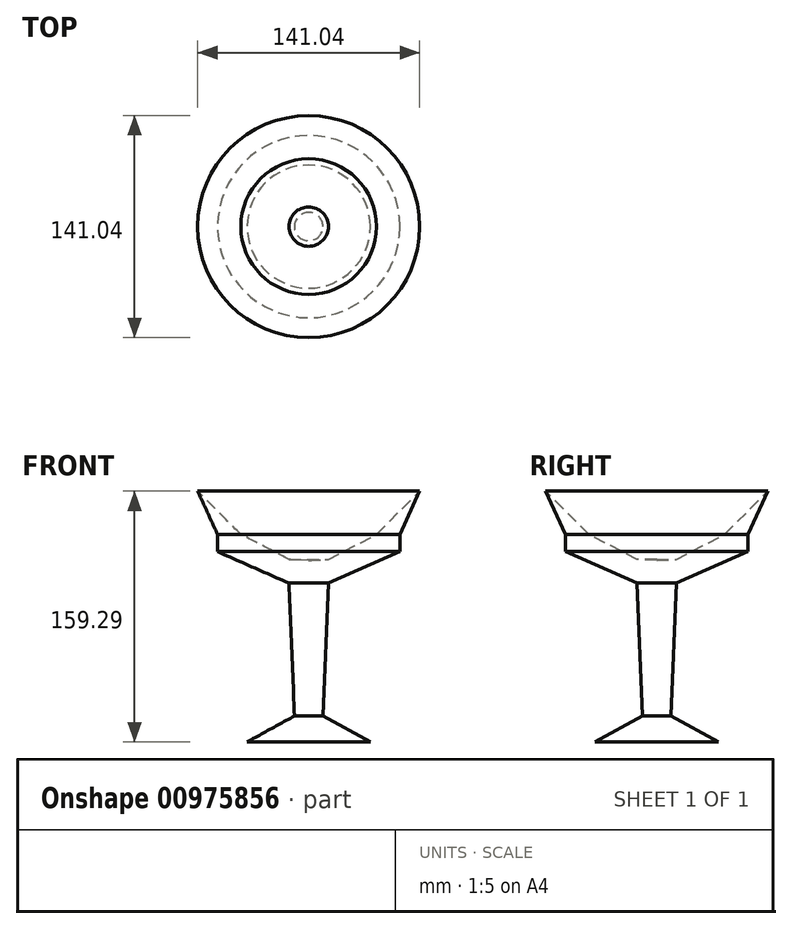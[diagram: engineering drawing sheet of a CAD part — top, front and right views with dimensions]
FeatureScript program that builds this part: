
annotation { "Feature Type Name" : "Feature", "Feature Type Description" : "" }
export const myFeature = defineFeature(function(context is Context, id is Id, definition is map)
    precondition{}
    {
        {
            var Q0;
            Q0=qCreatedBy(makeId("Front.planeOp"),FACE);
            var sketch = newSketch(context, id + "F0", { "sketchPlane" : qUnion([Q0])});
            skLineSegment(sketch, "E0", {"start": v(0, 79.46) * mm, "end": v(0, -77.08) * mm, "construction": true});
            skLineSegment(sketch, "E1", {"start": v(0, -61.15) * mm, "end": v(-39.11, -61.15) * mm});
            skLineSegment(sketch, "E2", {"start": v(-39.11, -61.15) * mm, "end": v(-9.05, -44.68) * mm});
            skLineSegment(sketch, "E3", {"start": v(-9.05, -44.68) * mm, "end": v(-12.5, 39.68) * mm});
            skLineSegment(sketch, "E4", {"start": v(-12.5, 39.68) * mm, "end": v(-57.9, 59.69) * mm});
            skLineSegment(sketch, "E5", {"start": v(-57.9, 59.69) * mm, "end": v(-57.9, 70.67) * mm});
            skLineSegment(sketch, "E6", {"start": v(-57.9, 70.67) * mm, "end": v(-70.52, 98.14) * mm});
            skLineSegment(sketch, "E7", {"start": v(-70.52, 98.14) * mm, "end": v(-43.08, 70.67) * mm});
            skLineSegment(sketch, "E8", {"start": v(-43.08, 70.67) * mm, "end": v(-12.5, 54.74) * mm});
            skLineSegment(sketch, "E9", {"start": v(-12.5, 54.74) * mm, "end": v(0, 54.2) * mm});
            skSolve(sketch);
        }
        {
            var Q0;
            Q0=sQuery(id+"F0.wireOp",EDGE,"E8");
            var Q1;
            Q1=sQuery(id+"F0.wireOp",EDGE,"E2");
            var Q2;
            Q2=sQuery(id+"F0.wireOp",EDGE,"E4");
            var Q3;
            Q3=sQuery(id+"F0.wireOp",EDGE,"E7");
            var Q4;
            Q4=sQuery(id+"F0.wireOp",EDGE,"E6");
            var Q5;
            Q5=sQuery(id+"F0.wireOp",EDGE,"E3");
            var Q6;
            Q6=sQuery(id+"F0.wireOp",EDGE,"E5");
            var Q7;
            Q7=sQuery(id+"F0.wireOp",EDGE,"E1");
            var Q8;
            Q8=sQuery(id+"F0.wireOp",EDGE,"E9");
            var Q9;
            Q9=sQuery(id+"F0.wireOp",EDGE,"E0");
            revolve(context, id + "F1", {"bodyType" : ToolBodyType.SURFACE, "surfaceOperationType" : NewSurfaceOperationType.NEW, "surfaceEntities" : qUnion([Q0, Q1, Q2, Q3, Q4, Q5, Q6, Q7, Q8]), "axis" : qUnion([Q9]), "revolveType" : RevolveType.FULL});
        }
    });
